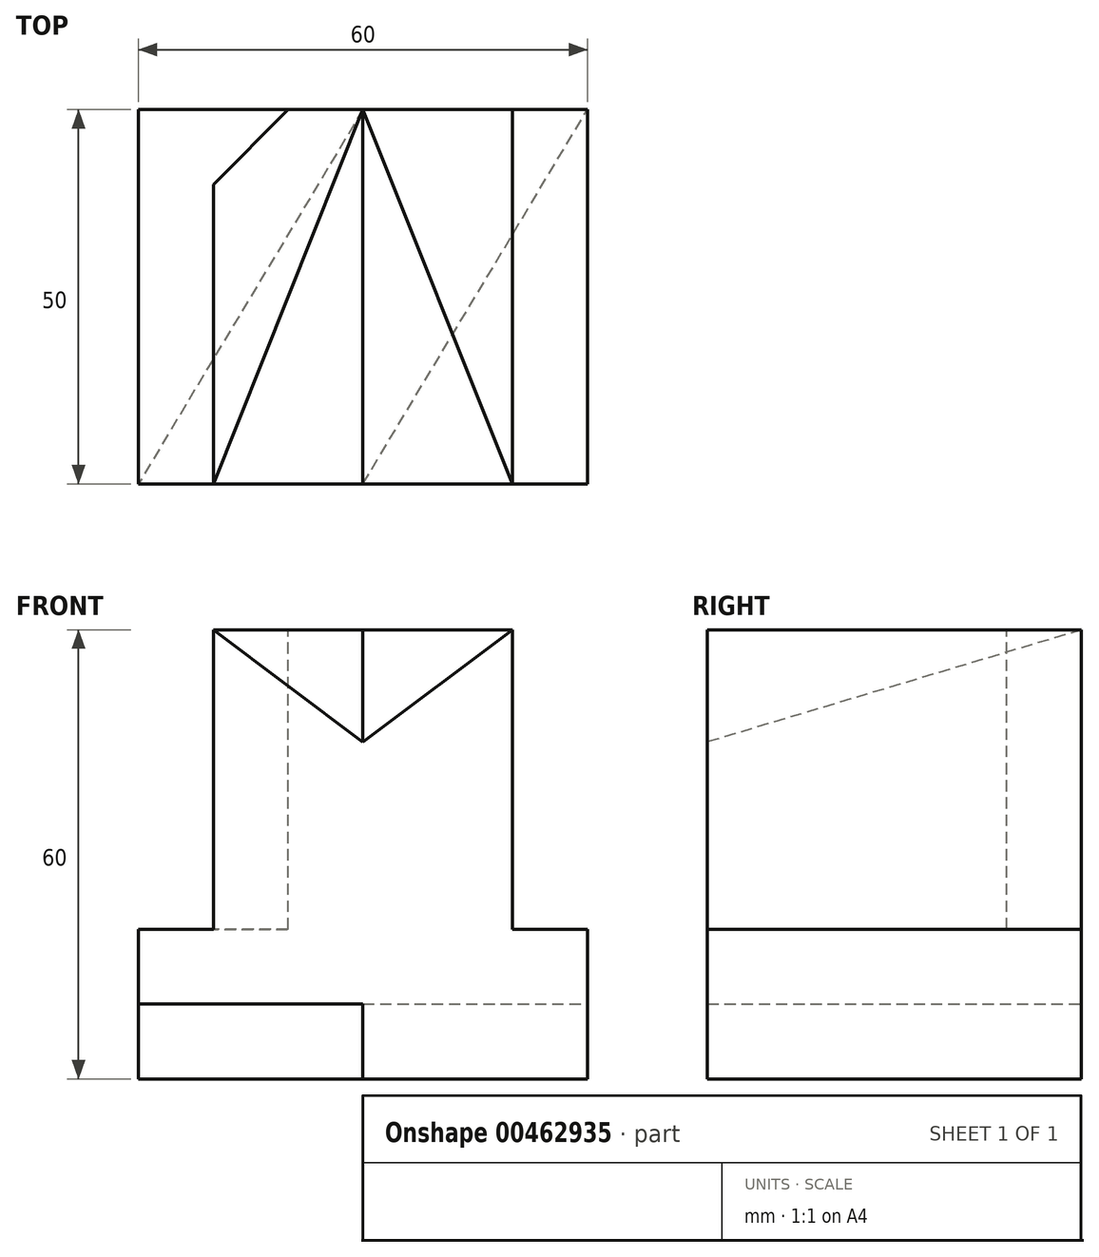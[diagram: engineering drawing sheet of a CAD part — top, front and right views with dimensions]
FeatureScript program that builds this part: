
annotation { "Feature Type Name" : "Feature", "Feature Type Description" : "" }
export const myFeature = defineFeature(function(context is Context, id is Id, definition is map)
    precondition{}
    {
        {
            var Q0;
            Q0=qCreatedBy(makeId("Top.planeOp"),FACE);
            var sketch = newSketch(context, id + "F0", { "sketchPlane" : qUnion([Q0])});
            skLineSegment(sketch, "E0.bottom", {"start": v(0, 0) * mm, "end": v(60, 0) * mm});
            skLineSegment(sketch, "E0.top", {"start": v(0, 50) * mm, "end": v(60, 50) * mm});
            skLineSegment(sketch, "E0.left", {"start": v(0, 0) * mm, "end": v(0, 50) * mm});
            skLineSegment(sketch, "E0.right", {"start": v(60, 0) * mm, "end": v(60, 50) * mm});
            skSolve(sketch);
        }
        {
            var Q0;
            Q0 = qSketchRegion(id + "F0", true);
            extrude(context, id + "F1", {"entities" : qUnion([Q0]), "depth" : 20 * mm});
        }
        {
            var Q0;
            Q0=makeQuery(id+"F1.opExtrude","CAP_FACE",FACE,{"disambiguationData":[OSD([sQuery(id+"F0.wireOp",EDGE,"E0.bottom"),sQuery(id+"F0.wireOp",EDGE,"E0.top"),sQuery(id+"F0.wireOp",EDGE,"E0.left"),sQuery(id+"F0.wireOp",EDGE,"E0.right")])],"isStart":false});
            var sketch = newSketch(context, id + "F2", { "sketchPlane" : qUnion([Q0])});
            skLineSegment(sketch, "E1", {"start": v(0, 0) * mm, "end": v(10, 0) * mm});
            skLineSegment(sketch, "E2.bottom", {"start": v(10, 0) * mm, "end": v(50, 0) * mm});
            skLineSegment(sketch, "E2.top", {"start": v(10, 50) * mm, "end": v(50, 50) * mm});
            skLineSegment(sketch, "E2.left", {"start": v(10, 0) * mm, "end": v(10, 50) * mm});
            skLineSegment(sketch, "E2.right", {"start": v(50, 0) * mm, "end": v(50, 50) * mm});
            skSolve(sketch);
        }
        {
            var Q0;
            Q0 = qSketchRegion(id + "F2", true);
            extrude(context, id + "F3", {"entities" : qUnion([Q0]), "operationType" : NewBodyOperationType.ADD, "depth" : 40 * mm});
        }
        {
            var Q0;
            Q0=makeQuery(id+"F1.opExtrude","CAP_FACE",FACE,{"disambiguationData":[OSD([sQuery(id+"F0.wireOp",EDGE,"E0.bottom"),sQuery(id+"F0.wireOp",EDGE,"E0.top"),sQuery(id+"F0.wireOp",EDGE,"E0.left"),sQuery(id+"F0.wireOp",EDGE,"E0.right")])],"isStart":true});
            var sketch = newSketch(context, id + "F4", { "sketchPlane" : qUnion([Q0])});
            skLineSegment(sketch, "E3", {"start": v(0, 0) * mm, "end": v(30, 0) * mm});
            skLineSegment(sketch, "E4", {"start": v(30, 0) * mm, "end": v(60, -50) * mm});
            skLineSegment(sketch, "E5", {"start": v(60, -50) * mm, "end": v(30, -50) * mm});
            skLineSegment(sketch, "E6", {"start": v(30, -50) * mm, "end": v(0, 0) * mm});
            skSolve(sketch);
        }
        {
            var Q0;
            Q0 = qSketchRegion(id + "F4", true);
            extrude(context, id + "F5", {"entities" : qUnion([Q0]), "operationType" : NewBodyOperationType.REMOVE, "oppositeDirection" : true, "depth" : 10 * mm});
        }
        {
            var Q0;
            Q0=makeQuery(id+"F3.opExtrude","CAP_FACE",FACE,{"disambiguationData":[OSD([sQuery(id+"F2.wireOp",EDGE,"E2.bottom"),sQuery(id+"F2.wireOp",EDGE,"E2.top"),sQuery(id+"F2.wireOp",EDGE,"E2.left"),sQuery(id+"F2.wireOp",EDGE,"E2.right")])],"isStart":false});
            var sketch = newSketch(context, id + "F6", { "sketchPlane" : qUnion([Q0])});
            skLineSegment(sketch, "E7", {"start": v(10, 50) * mm, "end": v(10, 40) * mm});
            skLineSegment(sketch, "E8", {"start": v(10, 50) * mm, "end": v(20, 50) * mm});
            skLineSegment(sketch, "E9", {"start": v(20, 50) * mm, "end": v(10, 40) * mm});
            skSolve(sketch);
        }
        {
            var Q0;
            Q0 = qSketchRegion(id + "F6", true);
            extrude(context, id + "F7", {"entities" : qUnion([Q0]), "operationType" : NewBodyOperationType.REMOVE, "oppositeDirection" : true, "depth" : 40 * mm, "offsetDistance" : 25 * mm});
        }
        {
            var Q0;
            Q0=makeQuery(id+"F3.opExtrude","CAP_FACE",FACE,{"disambiguationData":[OSD([sQuery(id+"F2.wireOp",EDGE,"E2.bottom"),sQuery(id+"F2.wireOp",EDGE,"E2.top"),sQuery(id+"F2.wireOp",EDGE,"E2.left"),sQuery(id+"F2.wireOp",EDGE,"E2.right")])],"isStart":false});
            var sketch = newSketch(context, id + "F8", { "sketchPlane" : qUnion([Q0])});
            skLineSegment(sketch, "E10", {"start": v(10, 0) * mm, "end": v(30, 0) * mm});
            skLineSegment(sketch, "E11", {"start": v(30, 0) * mm, "end": v(30, 50) * mm});
            skLineSegment(sketch, "E12", {"start": v(30, 50) * mm, "end": v(10, 0) * mm});
            skLineSegment(sketch, "E13", {"start": v(30, 50) * mm, "end": v(50, 0) * mm});
            skLineSegment(sketch, "E14", {"start": v(50, 0) * mm, "end": v(30, 0) * mm});
            skSolve(sketch);
        }
        {
            var Q0;
            Q0=makeQuery(id+"F3.boolean.opBoolean","MERGE",FACE,{"derivedFrom":[makeQuery(id+"F1.opExtrude","SWEPT_FACE",FACE,{"disambiguationData":[OSD([sQuery(id+"F0.wireOp",EDGE,"E0.bottom")])]}),makeQuery(id+"F3.opExtrude","SWEPT_FACE",FACE,{"disambiguationData":[OSD([sQuery(id+"F2.wireOp",EDGE,"E2.bottom")])]})]});
            var sketch = newSketch(context, id + "F9", { "sketchPlane" : qUnion([Q0])});
            skLineSegment(sketch, "E15", {"start": v(10, 60) * mm, "end": v(30, 60) * mm});
            skLineSegment(sketch, "E16", {"start": v(30, 60) * mm, "end": v(30, 45) * mm});
            skLineSegment(sketch, "E17", {"start": v(10, 60) * mm, "end": v(30, 45) * mm});
            skLineSegment(sketch, "E18", {"start": v(50, 60) * mm, "end": v(30, 45) * mm});
            skLineSegment(sketch, "E19", {"start": v(30, 60) * mm, "end": v(50, 60) * mm});
            skSolve(sketch);
        }
        {
            var Q0;
            Q0=sQuery(id+"F8.wireOp",VERTEX,"E11.end");
            var Q1;
            Q1=sQuery(id+"F9.wireOp",VERTEX,"E16.start");
            var Q2;
            Q2=sQuery(id+"F9.wireOp",VERTEX,"E16.end");
            cPlane(context, id + "F10", {"entities" : qUnion([Q0, Q1, Q2]), "cplaneType" : CPlaneType.THREE_POINT, "offset" : 25 * mm, "width" : 150 * mm, "height" : 150 * mm});
        }
        {
            var Q0;
            Q0=qCreatedBy(id+"F10.planeOp",FACE);
            var sketch = newSketch(context, id + "F11", { "sketchPlane" : qUnion([Q0])});
            skLineSegment(sketch, "E20", {"start": v(0, 60) * mm, "end": v(-50, 60) * mm});
            skLineSegment(sketch, "E21", {"start": v(0, 60) * mm, "end": v(0, 45) * mm});
            skLineSegment(sketch, "E22", {"start": v(0, 45) * mm, "end": v(-50, 60) * mm});
            skSolve(sketch);
        }
        {
            var Q0;
            Q0=makeQuery(id+"F8.imprint","IMPRINT",FACE,{"disambiguationData":[TD([[makeQuery(id+"F8.imprint","IMPRINT",EDGE,{"derivedFrom":sQuery(id+"F8.wireOp",EDGE,"E10")}),1.0]])]});
            var Q1;
            Q1=makeQuery(id+"F8.imprint","IMPRINT",FACE,{"disambiguationData":[TD([[makeQuery(id+"F8.imprint","IMPRINT",EDGE,{"derivedFrom":sQuery(id+"F8.wireOp",EDGE,"E11")}),-1.0]])]});
            var Q2;
            Q2=sQuery(id+"F11.wireOp",EDGE,"E22");
            sweep(context, id + "F12", {"operationType" : NewBodyOperationType.REMOVE, "profiles" : qUnion([Q0, Q1]), "path" : qUnion([Q2])});
        }
    });
